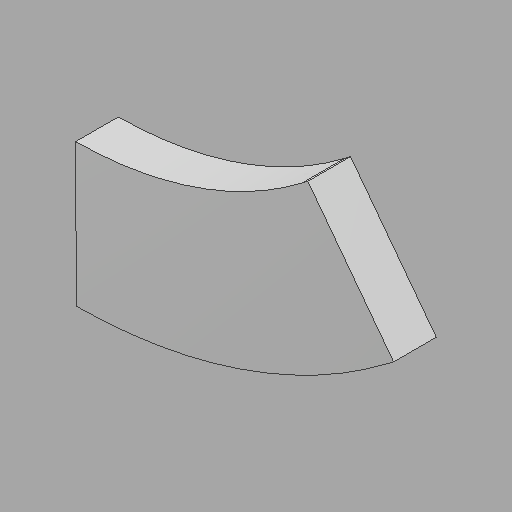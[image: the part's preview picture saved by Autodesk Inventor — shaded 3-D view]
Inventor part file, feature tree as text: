
AUTODESK INVENTOR PART (.ipt)
format: ipt  version: 2022.1 (Build 261234020, 234B)  size: 88,576 bytes
history: imported  units: in
note: dims shown in document units (in); Inventor stores cm internally (conversion verified against a paired STEP export)
features: imported_body x1
ambient origin geometry x8: Origin, YZ Plane, XZ Plane, XY Plane, X Axis, Y Axis, Z Axis, Center Point
bodies: Solid1 (imported_parasolid)
feature tree (1):
  imported_body  NMx_Import_Brep_tag  [imported B-rep: ~8 faces, bbox_mm=[1135.214774, 799.745127, 152.4]]
